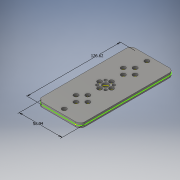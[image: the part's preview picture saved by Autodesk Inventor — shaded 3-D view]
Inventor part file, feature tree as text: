
AUTODESK INVENTOR PART (.ipt)
format: ipt  version: 2016 (Build 200138000, 138)  size: 186,368 bytes
history: native  units: mm
features: reference x19, sketch x2, extrude x1, hole x1, projected_geometry x1
ambient origin geometry x8: Origin, YZ Plane, XZ Plane, XY Plane, X Axis, Y Axis, Z Axis, Center Point
bodies: Body1 (feature_tree)
feature tree (24):
  extrude  "Extrusion2"  Depth=126.62mm
  hole  "Hole2"  [1 undecoded]
  sketch  "Sketch1"  dims[d9=6.0mm d10=0.0mm]
  reference  "Reference1"
  reference  "Reference2"
  reference  "Reference3"
  reference  "Reference4"
  reference  "Reference5"
  reference  "Reference6"
  reference  "Reference7"
  reference  "Reference8"
  reference  "Reference9"
  reference  "Reference10"
  reference  "Reference11"
  reference  "Reference12"
  reference  "Reference13"
  reference  "Reference14"
  reference  "Reference15"
  reference  "Reference16"
  reference  "Reference17"
  reference  "Reference18"
  reference  "Reference19"
  sketch  "Sketch3"  dims[d11=3.7mm d12=6.0mm d13=6.0mm d14=3.5mm d15=90.0deg d16=8.0mm d17=20.594885mm d18=126.62mm d19=58.04mm]
  projected_geometry  "Projected Loop1"
note: 1 required parameter value undecoded (feature->parameter linkage not recoverable at this tier; creation-order binding heuristic only, values carry confidence <= 0.55)
